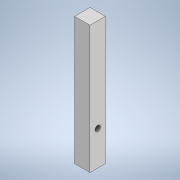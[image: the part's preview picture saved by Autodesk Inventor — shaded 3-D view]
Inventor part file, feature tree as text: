
AUTODESK INVENTOR PART (.ipt)
format: ipt  version: 2020.2 (Build 242310000, 310)  size: 102,400 bytes
history: native  units: mm
features: sketch x2, extrude x1, hole x1
ambient origin geometry x8: Origin, YZ Plane, XZ Plane, XY Plane, X Axis, Y Axis, Z Axis, Center Point
bodies: Solid1 (feature_tree)
feature tree (4):
  extrude  "Extrusion1"  Depth=83.2mm
  hole  "Hole1"  [1 undecoded]
  sketch  "Sketch1"  dims[d0=10.0mm d1=83.2mm]
  sketch  "Sketch2"  dims[d2=10.0mm d3=0.0mm d4=60.8mm d5=3.6mm d6=6.0mm d7=6.3mm d8=2.0mm d9=90.0deg d10=8.0mm d11=0.0mm]
note: 1 required parameter value undecoded (feature->parameter linkage not recoverable at this tier; creation-order binding heuristic only, values carry confidence <= 0.55)
